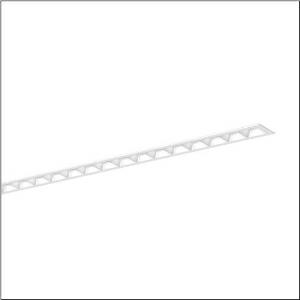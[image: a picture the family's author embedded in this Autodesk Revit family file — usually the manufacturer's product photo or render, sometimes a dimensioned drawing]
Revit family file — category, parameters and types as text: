
# Revit family: silica_r__21_51mx16db45wb_49d2
name_source: partatom
category: Lighting Fixtures
units: mm (PartAtom-declared; Revit-internal decimal feet)

## family parameters
Cut with Voids When Loaded = No
Host = Face
Light Source = No
Part Type = Normal
Room Calculation Point = No
Round Connector Dimension = Use Diameter
Shared = No

## types (1)
- --- (1 x LED, 5400 lm, 29.3 W, 4000K)
    Apparent Load = 29 VA
    CIE Flux Codes = 83 98 100 100 100
    Color Rendering = 80
    Color Temperature = 4000K
    Default Elevation = 1800 mm
    Description = Silica® 21, office luminaire, primary light control with darklight reflector, of PMMA, white, CAT 2 (L<= 3000cd/m²), light emission: direct distribution, primary light characteristic: symmetric, installation type: recessed, LED, rated luminous flux: 5.400lm, luminous efficacy: 184lm/W, light colour: 840, colour temperature: 4000K, control gear: DALI 2, with terminal, 3+2-pole, max. 2.5mm², mains connection: 220..240V, AC, 50/60Hz, rated input power: 29.3W, luminaire housing, of aluminium, traffic white (RAL 9016), length: 1.528mm, width: 79mm, height: 53mm, protection rating (complete): IP20, insulation class (complete): insulation class I (protective earthing), certification: CE, ENEC, VDE, permissible operating ambient temperature: 0..+35°C, standard: EN 50419, packaging unit: 1 piece
    Height = 0 mm  [stored 0 ft]
    Lamp = 1 x LED
    Lamp Light Flux = 5400 lm
    Lamp Power = 29.3 W
    Lamp count = 1
    Length = 1527 mm
    Luminous efficacy = 184 lm/W
    Manufacturer = Siteco
    ModVariant = No
    Model = 51MX16DB45WB
    Mounting Place = Ceiling
    Mounting Type = Recessed
    Number of Poles = 1
    OnlyDefault = Yes
    Power Factor = 1
    Product Name = Silica® 21
    Product group = office luminaire | ceiling recessed
    ProductGroupID = 400
    Protection Class = Protection class I
    Protection Degree = IP 20
    RLX_Detail_Level = 1
    RLX_Emergency_Light_Flux = 0 lm
    RLX_Emergency_Type = 0
    RLX_Emergency_Type_DB = No
    RlxData = <blob elided: 39485 chars, md5=75aab98e>
    Socket = socket
    Standby Power = 0 W
    System Light Flux = 5400 lm
    System Power = 29 W
    Type Comments = factory setting: luminous flux: 100 % | dim-lin: 254 | 336 mA
    Type Image = l_1335884.jpg
    URL = http://relux.com
    VarID = @adj_145647
    Voltage = 0 V
    Weight = 0.00 kg
    Width = 79 mm

note: [stored X ft] marks values corroborated as IEEE doubles in the binary element streams (Revit-internal decimal feet)

## geometry (parser evidence)
native form markers: Blend x4, Sweep x10
no freeform markers — native parametric forms only
